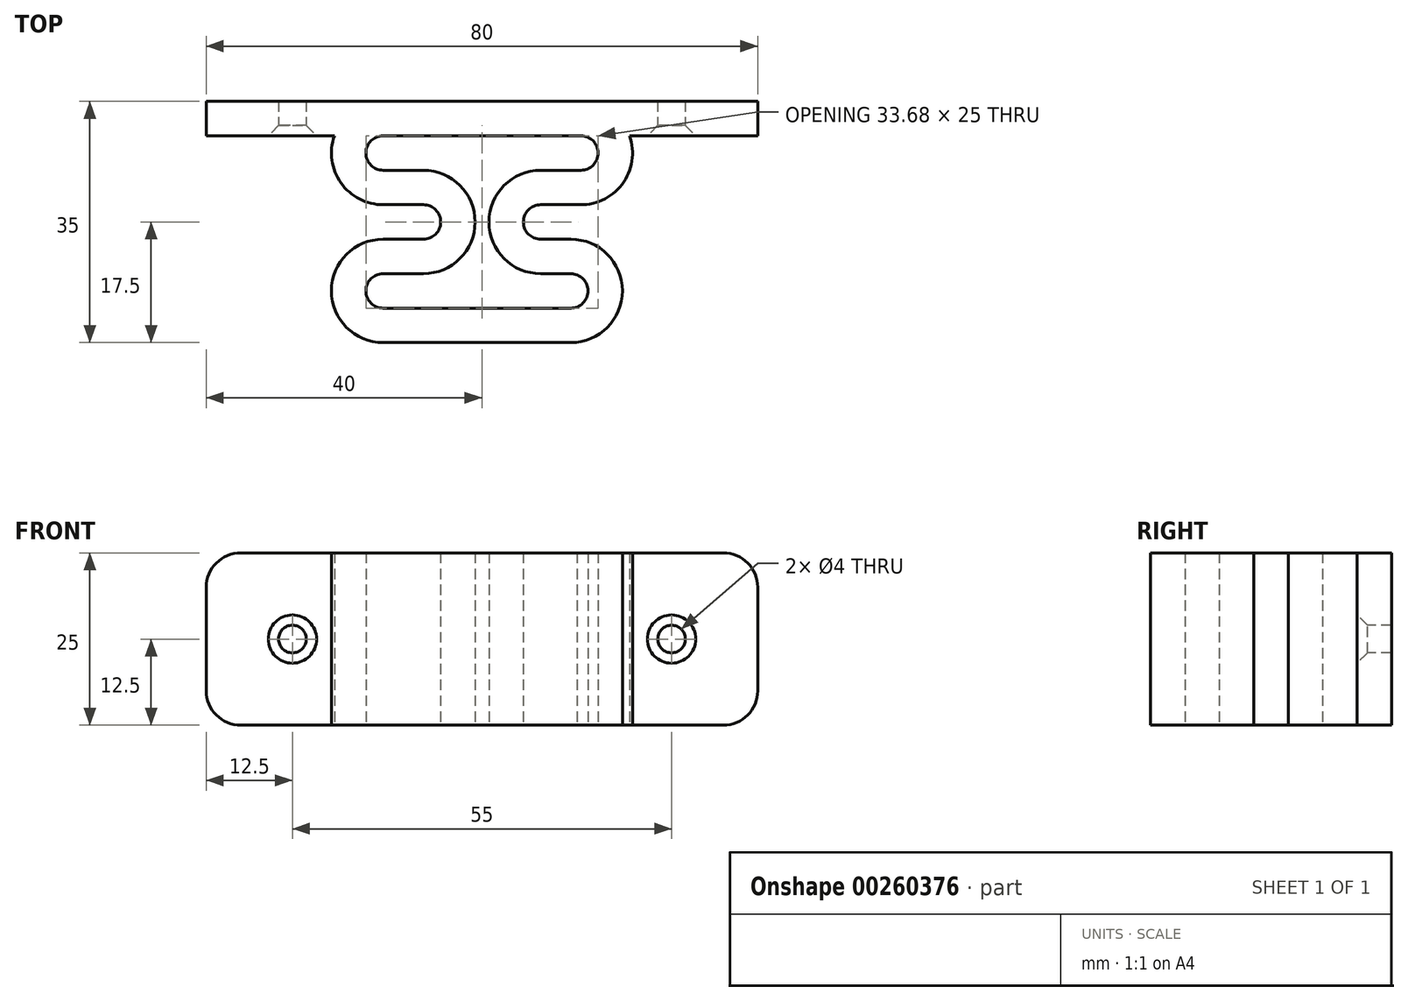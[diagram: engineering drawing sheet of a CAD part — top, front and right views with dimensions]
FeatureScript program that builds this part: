
annotation { "Feature Type Name" : "Feature", "Feature Type Description" : "" }
export const myFeature = defineFeature(function(context is Context, id is Id, definition is map)
    precondition{}
    {
        {
            var Q0;
            Q0=qCreatedBy(makeId("Top.planeOp"),FACE);
            var sketch = newSketch(context, id + "F0", { "sketchPlane" : qUnion([Q0])});
            skCircle(sketch, "E0", {"center": v(-14.34, 10) * mm, "radius": 2.5 * mm});
            skCircle(sketch, "E1", {"center": v(-14.34, 10) * mm, "radius": 7.5 * mm});
            skCircle(sketch, "E2", {"center": v(14.34, 10) * mm, "radius": 7.5 * mm});
            skCircle(sketch, "E3", {"center": v(14.34, 10) * mm, "radius": 2.5 * mm});
            skLineSegment(sketch, "E4", {"start": v(-14.34, 17.5) * mm, "end": v(14.34, 17.5) * mm});
            skPoint(sketch, "E5", {"position": v(0, 17.5) * mm});
            skLineSegment(sketch, "E6", {"start": v(-14.34, 12.5) * mm, "end": v(14.34, 12.5) * mm});
            skCircle(sketch, "E7", {"center": v(-14.34, -10) * mm, "radius": 2.5 * mm});
            skCircle(sketch, "E8", {"center": v(-14.34, -10) * mm, "radius": 7.5 * mm});
            skCircle(sketch, "E9", {"center": v(12.87, -10) * mm, "radius": 2.5 * mm});
            skCircle(sketch, "E10", {"center": v(12.87, -10) * mm, "radius": 7.5 * mm});
            skLineSegment(sketch, "E11", {"start": v(-14.34, -17.5) * mm, "end": v(12.87, -17.5) * mm});
            skLineSegment(sketch, "E12", {"start": v(-14.34, -12.5) * mm, "end": v(12.87, -12.5) * mm});
            skCircle(sketch, "E13", {"center": v(-8.5, 0) * mm, "radius": 2.5 * mm});
            skCircle(sketch, "E14", {"center": v(8.5, 0) * mm, "radius": 2.5 * mm});
            skCircle(sketch, "E15", {"center": v(-8.5, 0) * mm, "radius": 7.5 * mm});
            skCircle(sketch, "E16", {"center": v(8.5, 0) * mm, "radius": 7.5 * mm});
            skLineSegment(sketch, "E17", {"start": v(-14.34, 7.5) * mm, "end": v(-8.5, 7.5) * mm});
            skLineSegment(sketch, "E18", {"start": v(14.34, 7.5) * mm, "end": v(8.5, 7.5) * mm});
            skLineSegment(sketch, "E19", {"start": v(-8.5, 2.5) * mm, "end": v(-14.34, 2.5) * mm});
            skLineSegment(sketch, "E20", {"start": v(8.5, 2.5) * mm, "end": v(13.8, 2.52) * mm});
            skLineSegment(sketch, "E21", {"start": v(-8.5, -2.5) * mm, "end": v(-14.34, -2.5) * mm});
            skLineSegment(sketch, "E22", {"start": v(8.5, -2.5) * mm, "end": v(12.87, -2.5) * mm});
            skLineSegment(sketch, "E23", {"start": v(-14.34, -7.5) * mm, "end": v(-8.5, -7.5) * mm});
            skLineSegment(sketch, "E24", {"start": v(8.5, -7.5) * mm, "end": v(12.87, -7.5) * mm});
            skSolve(sketch);
        }
        {
            var Q0;
            {var subQ0=sQuery(id+"F0.wireOp",EDGE,"E4");Q0=makeQuery(id+"F0.imprint","IMPRINT",FACE,{"disambiguationData":[TD([[makeQuery(id+"F0.imprint","IMPRINT",EDGE,{"derivedFrom":subQ0}),-1.0]])]});}
            var Q1;
            {var subQ0=sQuery(id+"F0.wireOp",EDGE,"E1");var subQ2=sQuery(id+"F0.wireOp",EDGE,"8CR9bk30-KQ4b-ltya-m7mn-kqcPntCiqzbD");var subQ3=makeQuery(id+"F0.imprint","INTERSECT",VERTEX,{"disambiguationData":[OD(0.0)],"derivedFrom":[subQ2,subQ0]});Q1=makeQuery(id+"F0.imprint","IMPRINT",FACE,{"disambiguationData":[TD([[makeQuery(id+"F0.imprint","IMPRINT",EDGE,{"disambiguationData":[TD([[subQ3,1.0]])],"derivedFrom":subQ2}),-1.0]])]});}
            var Q2;
            {var subQ0=sQuery(id+"F0.wireOp",EDGE,"8CR9bk30-KQ4b-ltya-m7mn-kqcPntCiqzbD");var subQ1=makeQuery(id+"F0.imprint","INTERSECT",VERTEX,{"derivedFrom":[subQ0,sQuery(id+"F0.wireOp",EDGE,"E0")]});Q2=makeQuery(id+"F0.imprint","IMPRINT",FACE,{"disambiguationData":[TD([[makeQuery(id+"F0.imprint","IMPRINT",EDGE,{"disambiguationData":[TD([[subQ1,1.0]])],"derivedFrom":subQ0}),1.0]])]});}
            var Q3;
            {var subQ0=sQuery(id+"F0.wireOp",EDGE,"E1");var subQ1=sQuery(id+"F0.wireOp",EDGE,"6h7cOsYY-HjXx-50Em-QmnM-c8Dnv7Tza03D");var subQ2=makeQuery(id+"F0.imprint","INTERSECT",VERTEX,{"derivedFrom":[subQ1,subQ0]});Q3=makeQuery(id+"F0.imprint","IMPRINT",FACE,{"disambiguationData":[TD([[makeQuery(id+"F0.imprint","IMPRINT",EDGE,{"disambiguationData":[TD([[subQ2,1.0]])],"derivedFrom":subQ1}),-1.0]])]});}
            var Q4;
            {var subQ0=sQuery(id+"F0.wireOp",EDGE,"E8");var subQ1=sQuery(id+"F0.wireOp",EDGE,"8CR9bk30-KQ4b-ltya-m7mn-kqcPntCiqzbD");var subQ2=makeQuery(id+"F0.imprint","INTERSECT",VERTEX,{"disambiguationData":[OD(0.0)],"derivedFrom":[subQ1,subQ0]});Q4=makeQuery(id+"F0.imprint","IMPRINT",FACE,{"disambiguationData":[TD([[makeQuery(id+"F0.imprint","IMPRINT",EDGE,{"disambiguationData":[TD([[subQ2,-1.0]])],"derivedFrom":subQ1}),1.0]])]});}
            var Q5;
            {var subQ0=sQuery(id+"F0.wireOp",EDGE,"E8");var subQ4=sQuery(id+"F0.wireOp",EDGE,"8CR9bk30-KQ4b-ltya-m7mn-kqcPntCiqzbD");var subQ5=makeQuery(id+"F0.imprint","INTERSECT",VERTEX,{"disambiguationData":[OD(0.0)],"derivedFrom":[subQ4,subQ0]});Q5=makeQuery(id+"F0.imprint","IMPRINT",FACE,{"disambiguationData":[TD([[makeQuery(id+"F0.imprint","IMPRINT",EDGE,{"disambiguationData":[TD([[subQ5,-1.0]])],"derivedFrom":subQ4}),-1.0]])]});}
            var Q6;
            {var subQ0=sQuery(id+"F0.wireOp",EDGE,"E11");Q6=makeQuery(id+"F0.imprint","IMPRINT",FACE,{"disambiguationData":[TD([[makeQuery(id+"F0.imprint","IMPRINT",EDGE,{"derivedFrom":subQ0}),1.0]])]});}
            var Q7;
            {var subQ0=sQuery(id+"F0.wireOp",EDGE,"E10");var subQ2=sQuery(id+"F0.wireOp",EDGE,"DIOqt0p8-QBxR-8iWn-KdwK-cJBDFyHMyHgb");var subQ3=makeQuery(id+"F0.imprint","INTERSECT",VERTEX,{"disambiguationData":[OD(0.0)],"derivedFrom":[subQ2,subQ0]});Q7=makeQuery(id+"F0.imprint","IMPRINT",FACE,{"disambiguationData":[TD([[makeQuery(id+"F0.imprint","IMPRINT",EDGE,{"disambiguationData":[TD([[subQ3,1.0]])],"derivedFrom":subQ2}),-1.0]])]});}
            var Q8;
            {var subQ0=sQuery(id+"F0.wireOp",EDGE,"E10");var subQ1=sQuery(id+"F0.wireOp",EDGE,"DIOqt0p8-QBxR-8iWn-KdwK-cJBDFyHMyHgb");var subQ2=makeQuery(id+"F0.imprint","INTERSECT",VERTEX,{"disambiguationData":[OD(1.0)],"derivedFrom":[subQ1,subQ0]});Q8=makeQuery(id+"F0.imprint","IMPRINT",FACE,{"disambiguationData":[TD([[makeQuery(id+"F0.imprint","IMPRINT",EDGE,{"disambiguationData":[TD([[subQ2,-1.0]])],"derivedFrom":subQ1}),1.0]])]});}
            var Q9;
            {var subQ0=sQuery(id+"F0.wireOp",EDGE,"DIOqt0p8-QBxR-8iWn-KdwK-cJBDFyHMyHgb");var subQ1=sQuery(id+"F0.wireOp",EDGE,"E2");var subQ2=makeQuery(id+"F0.imprint","INTERSECT",VERTEX,{"disambiguationData":[OD(1.0)],"derivedFrom":[subQ1,subQ0]});Q9=makeQuery(id+"F0.imprint","IMPRINT",FACE,{"disambiguationData":[TD([[makeQuery(id+"F0.imprint","IMPRINT",EDGE,{"disambiguationData":[TD([[subQ2,-1.0]])],"derivedFrom":subQ1}),-1.0]])]});}
            var Q10;
            {var subQ1=sQuery(id+"F0.wireOp",EDGE,"E2");var subQ7=makeQuery(id+"F0.imprint","INTERSECT",VERTEX,{"derivedFrom":[subQ1,sQuery(id+"F0.wireOp",EDGE,"E4")]});Q10=makeQuery(id+"F0.imprint","IMPRINT",FACE,{"disambiguationData":[TD([[makeQuery(id+"F0.imprint","IMPRINT",EDGE,{"disambiguationData":[TD([[subQ7,-1.0]])],"derivedFrom":subQ1}),1.0]])]});}
            var Q11;
            {var subQ0=sQuery(id+"F0.wireOp",EDGE,"DIOqt0p8-QBxR-8iWn-KdwK-cJBDFyHMyHgb");var subQ1=sQuery(id+"F0.wireOp",EDGE,"E2");var subQ2=makeQuery(id+"F0.imprint","INTERSECT",VERTEX,{"disambiguationData":[OD(1.0)],"derivedFrom":[subQ1,subQ0]});Q11=makeQuery(id+"F0.imprint","IMPRINT",FACE,{"disambiguationData":[TD([[makeQuery(id+"F0.imprint","IMPRINT",EDGE,{"disambiguationData":[TD([[subQ2,-1.0]])],"derivedFrom":subQ1}),1.0]])]});}
            var Q12;
            {var subQ8=sQuery(id+"F0.wireOp",EDGE,"E17");Q12=makeQuery(id+"F0.imprint","IMPRINT",FACE,{"disambiguationData":[TD([[makeQuery(id+"F0.imprint","IMPRINT",EDGE,{"derivedFrom":subQ8}),-1.0]])]});}
            var Q13;
            {var subQ0=sQuery(id+"F0.wireOp",EDGE,"E1");var subQ1=makeQuery(id+"F0.imprint","INTERSECT",VERTEX,{"derivedFrom":[subQ0,sQuery(id+"F0.wireOp",EDGE,"E19")]});Q13=makeQuery(id+"F0.imprint","IMPRINT",FACE,{"disambiguationData":[TD([[makeQuery(id+"F0.imprint","IMPRINT",EDGE,{"disambiguationData":[TD([[subQ1,1.0]])],"derivedFrom":subQ0}),1.0]])]});}
            var Q14;
            {var subQ5=sQuery(id+"F0.wireOp",EDGE,"E19");Q14=makeQuery(id+"F0.imprint","IMPRINT",FACE,{"disambiguationData":[TD([[makeQuery(id+"F0.imprint","IMPRINT",EDGE,{"derivedFrom":subQ5}),-1.0]])]});}
            var Q15;
            {var subQ0=sQuery(id+"F0.wireOp",EDGE,"E8");var subQ1=makeQuery(id+"F0.imprint","INTERSECT",VERTEX,{"derivedFrom":[subQ0,sQuery(id+"F0.wireOp",EDGE,"E21")]});Q15=makeQuery(id+"F0.imprint","IMPRINT",FACE,{"disambiguationData":[TD([[makeQuery(id+"F0.imprint","IMPRINT",EDGE,{"disambiguationData":[TD([[subQ1,1.0]])],"derivedFrom":subQ0}),1.0]])]});}
            var Q16;
            {var subQ0=sQuery(id+"F0.wireOp",EDGE,"E10");var subQ1=makeQuery(id+"F0.imprint","INTERSECT",VERTEX,{"derivedFrom":[subQ0,sQuery(id+"F0.wireOp",EDGE,"E22")]});Q16=makeQuery(id+"F0.imprint","IMPRINT",FACE,{"disambiguationData":[TD([[makeQuery(id+"F0.imprint","IMPRINT",EDGE,{"disambiguationData":[TD([[subQ1,1.0]])],"derivedFrom":subQ0}),1.0]])]});}
            var Q17;
            {var subQ0=sQuery(id+"F0.wireOp",EDGE,"E2");var subQ1=makeQuery(id+"F0.imprint","INTERSECT",VERTEX,{"derivedFrom":[subQ0,sQuery(id+"F0.wireOp",EDGE,"E20")]});Q17=makeQuery(id+"F0.imprint","IMPRINT",FACE,{"disambiguationData":[TD([[makeQuery(id+"F0.imprint","IMPRINT",EDGE,{"disambiguationData":[TD([[subQ1,1.0]])],"derivedFrom":subQ0}),1.0]])]});}
            var Q18;
            {var subQ5=sQuery(id+"F0.wireOp",EDGE,"E20");Q18=makeQuery(id+"F0.imprint","IMPRINT",FACE,{"disambiguationData":[TD([[makeQuery(id+"F0.imprint","IMPRINT",EDGE,{"derivedFrom":subQ5}),1.0]])]});}
            var Q19;
            {var subQ8=sQuery(id+"F0.wireOp",EDGE,"E23");Q19=makeQuery(id+"F0.imprint","IMPRINT",FACE,{"disambiguationData":[TD([[makeQuery(id+"F0.imprint","IMPRINT",EDGE,{"derivedFrom":subQ8}),1.0]])]});}
            var Q20;
            {var subQ8=sQuery(id+"F0.wireOp",EDGE,"E24");Q20=makeQuery(id+"F0.imprint","IMPRINT",FACE,{"disambiguationData":[TD([[makeQuery(id+"F0.imprint","IMPRINT",EDGE,{"derivedFrom":subQ8}),1.0]])]});}
            extrude(context, id + "F1", {"entities" : qUnion([Q0, Q1, Q2, Q3, Q4, Q5, Q6, Q7, Q8, Q9, Q10, Q11, Q12, Q13, Q14, Q15, Q16, Q17, Q18, Q19, Q20]), "depth" : 25 * mm});
        }
        {
            var Q0;
            Q0=qCreatedBy(makeId("Right.planeOp"),FACE);
            var sketch = newSketch(context, id + "F2", { "sketchPlane" : qUnion([Q0])});
            skLineSegment(sketch, "E25.bottom", {"start": v(17.5, 25) * mm, "end": v(12.5, 25) * mm});
            skLineSegment(sketch, "E25.top", {"start": v(17.5, 0) * mm, "end": v(12.5, 0) * mm});
            skLineSegment(sketch, "E25.left", {"start": v(17.5, 25) * mm, "end": v(17.5, 0) * mm});
            skLineSegment(sketch, "E25.right", {"start": v(12.5, 25) * mm, "end": v(12.5, 0) * mm});
            skSolve(sketch);
        }
        {
            var Q0;
            Q0 = qSketchRegion(id + "F2", true);
            extrude(context, id + "F3", {"entities" : qUnion([Q0]), "operationType" : NewBodyOperationType.ADD, "endBound" : BoundingType.SYMMETRIC, "depth" : 80 * mm});
        }
        {
            var Q0;
            Q0=makeQuery(id+"F3.opExtrude","CAP_EDGE",EDGE,{"disambiguationData":[OSD([sQuery(id+"F2.wireOp",EDGE,"E25.top")])],"isStart":false});
            var Q1;
            Q1=makeQuery(id+"F3.opExtrude","CAP_EDGE",EDGE,{"disambiguationData":[OSD([sQuery(id+"F2.wireOp",EDGE,"E25.bottom")])],"isStart":false});
            var Q2;
            Q2=makeQuery(id+"F3.opExtrude","CAP_EDGE",EDGE,{"disambiguationData":[OSD([sQuery(id+"F2.wireOp",EDGE,"E25.bottom")])],"isStart":true});
            var Q3;
            Q3=makeQuery(id+"F3.opExtrude","CAP_EDGE",EDGE,{"disambiguationData":[OSD([sQuery(id+"F2.wireOp",EDGE,"E25.top")])],"isStart":true});
            fillet(context, id + "F4", {"entities" : qUnion([Q0, Q1, Q2, Q3]), "radius" : 5 * mm, "tangentPropagation" : true, "allowEdgeOverflow" : false});
        }
        {
            var Q0;
            {var subQ0=sQuery(id+"F0.wireOp",EDGE,"E1");var subQ25=sQuery(id+"F2.wireOp",EDGE,"E25.right");Q0=makeQuery(id+"F3.boolean.opBoolean","SPLIT",FACE,{"disambiguationData":[TD([makeQuery(id+"F1.opExtrude","SWEPT_FACE",FACE,{"disambiguationData":[OSD([subQ0])]})])],"derivedFrom":makeQuery(id+"F3.opExtrude","SWEPT_FACE",FACE,{"disambiguationData":[OSD([subQ25])]})});}
            var sketch = newSketch(context, id + "F5", { "sketchPlane" : qUnion([Q0])});
            skPoint(sketch, "E26", {"position": v(-27.5, 12.5) * mm});
            skPoint(sketch, "E27", {"position": v(27.5, 12.5) * mm});
            skPoint(sketch, "E28", {"position": v(-40, 12.5) * mm});
            skLineSegment(sketch, "E29", {"start": v(-40, 12.5) * mm, "end": v(-27.5, 12.5) * mm});
            skLineSegment(sketch, "E30", {"start": v(-27.5, 25) * mm, "end": v(-27.5, 12.5) * mm});
            skLineSegment(sketch, "E31", {"start": v(40, 12.5) * mm, "end": v(27.5, 12.5) * mm});
            skLineSegment(sketch, "E32", {"start": v(27.5, 12.5) * mm, "end": v(27.5, 25) * mm});
            skSolve(sketch);
        }
        {
            var Q0;
            Q0=sQuery(id+"F5.wireOp",VERTEX,"E27");
            var Q1;
            Q1=sQuery(id+"F5.wireOp",VERTEX,"E26");
            var Q2;
            Q2=makeQuery(id+"F1.opExtrude","SWEPT_BODY",BODY,{"disambiguationData":[OSD([sQuery(id+"F0.wireOp",EDGE,"E0"),sQuery(id+"F0.wireOp",EDGE,"E1"),sQuery(id+"F0.wireOp",EDGE,"E2"),sQuery(id+"F0.wireOp",EDGE,"E3"),sQuery(id+"F0.wireOp",EDGE,"E4"),sQuery(id+"F0.wireOp",EDGE,"E6"),sQuery(id+"F0.wireOp",EDGE,"E7"),sQuery(id+"F0.wireOp",EDGE,"E8"),sQuery(id+"F0.wireOp",EDGE,"E9"),sQuery(id+"F0.wireOp",EDGE,"E10"),sQuery(id+"F0.wireOp",EDGE,"E11"),sQuery(id+"F0.wireOp",EDGE,"E12"),sQuery(id+"F0.wireOp",EDGE,"E13"),sQuery(id+"F0.wireOp",EDGE,"E14"),sQuery(id+"F0.wireOp",EDGE,"E15"),sQuery(id+"F0.wireOp",EDGE,"E16"),sQuery(id+"F0.wireOp",EDGE,"E17"),sQuery(id+"F0.wireOp",EDGE,"E18"),sQuery(id+"F0.wireOp",EDGE,"E19"),sQuery(id+"F0.wireOp",EDGE,"E20"),sQuery(id+"F0.wireOp",EDGE,"E21"),sQuery(id+"F0.wireOp",EDGE,"E22"),sQuery(id+"F0.wireOp",EDGE,"E23"),sQuery(id+"F0.wireOp",EDGE,"E24")])]});
            hole(context, id + "F6", {"style" : HoleStyle.C_SINK, "endStyle" : HoleEndStyle.THROUGH, "holeDiameter" : 4 * mm, "cSinkDiameter" : 7 * mm, "cSinkAngle" : 90 * degree, "tappedDepth" : 13.2 * mm, "tapClearance" : 3, "startFromSketch" : true, "locations" : qUnion([Q0, Q1]), "scope" : qUnion([Q2])});
        }
    });
